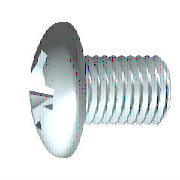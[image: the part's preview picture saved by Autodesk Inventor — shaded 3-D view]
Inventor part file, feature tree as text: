
AUTODESK INVENTOR PART (.ipt)
format: ipt  version: 2022 (Build 260153000, 153)  size: 341,504 bytes
history: native  units: mm (DEFAULTED — no unit token found)
features: other x2, plane x2, extrude x2
ambient origin geometry x7: Origin, YZ Plane, XZ Plane, X Axis, Y Axis, Z Axis, Center Point
bodies: Solid1 (feature_tree)
feature tree (6):
  other  "Базовый элемент"
  plane  "Work Plane1"
  extrude  "Паз"  Depth=3.5mm
  other  "Вырез"
  extrude  "Прорезь крестообразная"  Depth=1.93mm
  plane  "Work Plane3"
